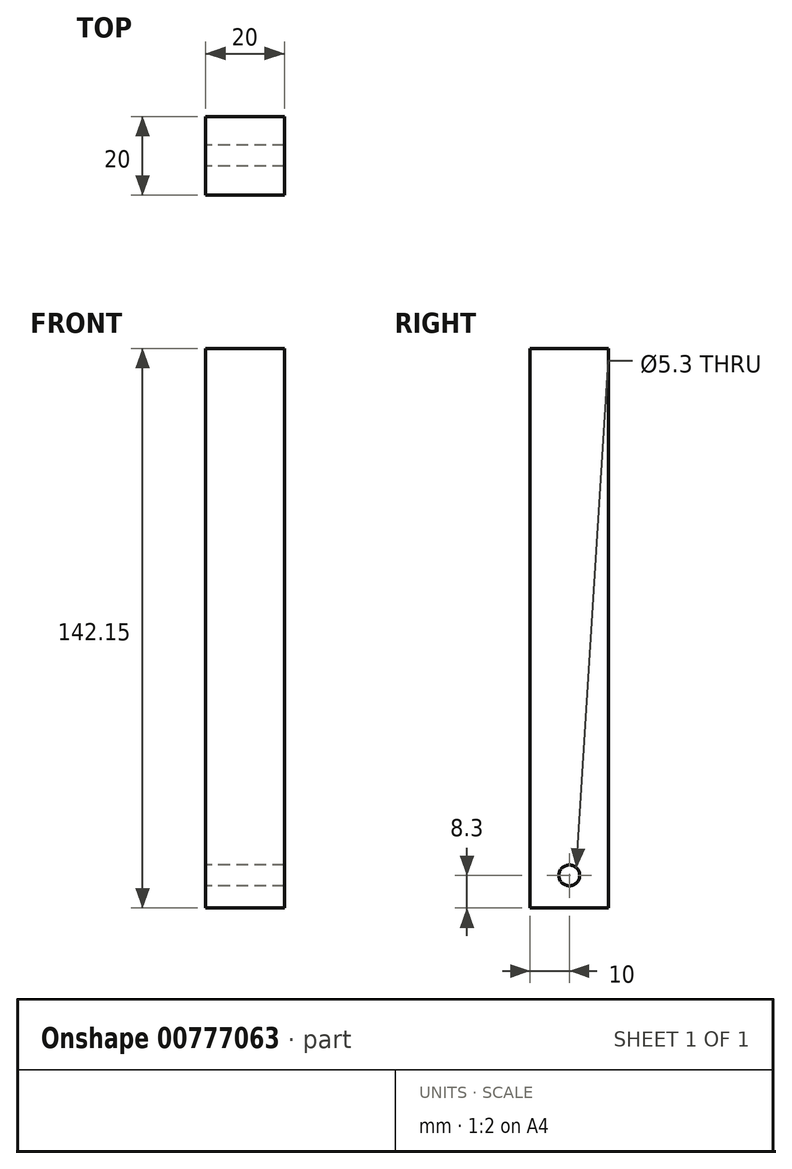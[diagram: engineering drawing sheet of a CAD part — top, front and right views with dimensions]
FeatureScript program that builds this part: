
annotation { "Feature Type Name" : "Feature", "Feature Type Description" : "" }
export const myFeature = defineFeature(function(context is Context, id is Id, definition is map)
    precondition{}
    {
        {
            var Q0;
            Q0=qCreatedBy(makeId("Top.planeOp"),FACE);
            var sketch = newSketch(context, id + "F0", { "sketchPlane" : qUnion([Q0])});
            skLineSegment(sketch, "E0.bottom", {"start": v(-10, 10) * mm, "end": v(10, 10) * mm});
            skLineSegment(sketch, "E0.top", {"start": v(-10, -10) * mm, "end": v(10, -10) * mm});
            skLineSegment(sketch, "E0.left", {"start": v(-10, 10) * mm, "end": v(-10, -10) * mm});
            skLineSegment(sketch, "E0.right", {"start": v(10, 10) * mm, "end": v(10, -10) * mm});
            skSolve(sketch);
        }
        {
            var Q0;
            Q0=qSketchRegion(id+"F0",true);
            extrude(context, id + "F1", {"entities" : qUnion([Q0]), "depth" : (132.15 + 10) * mm, "offsetDistance" : 25 * mm});
        }
        {
            var Q0;
            Q0=makeQuery(id+"F1.opExtrude","SWEPT_FACE",FACE,{"disambiguationData":[OSD([sQuery(id+"F0.wireOp",EDGE,"E0.right")])]});
            var sketch = newSketch(context, id + "F2", { "sketchPlane" : qUnion([Q0])});
            skCircle(sketch, "E1", {"center": v(0, 10) * mm, "radius": 2.5 * mm});
            skSolve(sketch);
        }
        {
            var Q0;
            Q0=makeQuery(id+"F1.opExtrude","SWEPT_FACE",FACE,{"disambiguationData":[OSD([sQuery(id+"F0.wireOp",EDGE,"E0.left")])]});
            var sketch = newSketch(context, id + "F3", { "sketchPlane" : qUnion([Q0])});
            skCircle(sketch, "E2", {"center": v(0, 8.3) * mm, "radius": 2.65 * mm});
            skPoint(sketch, "E2.centerSnap0", {"position": v(0, 142.15) * mm});
            skSolve(sketch);
        }
        {
            var Q0;
            Q0=qSketchRegion(id+"F3",true);
            extrude(context, id + "F4", {"entities" : qUnion([Q0]), "operationType" : NewBodyOperationType.REMOVE, "endBound" : BoundingType.THROUGH_ALL, "oppositeDirection" : true, "depth" : 25 * mm});
        }
    });
